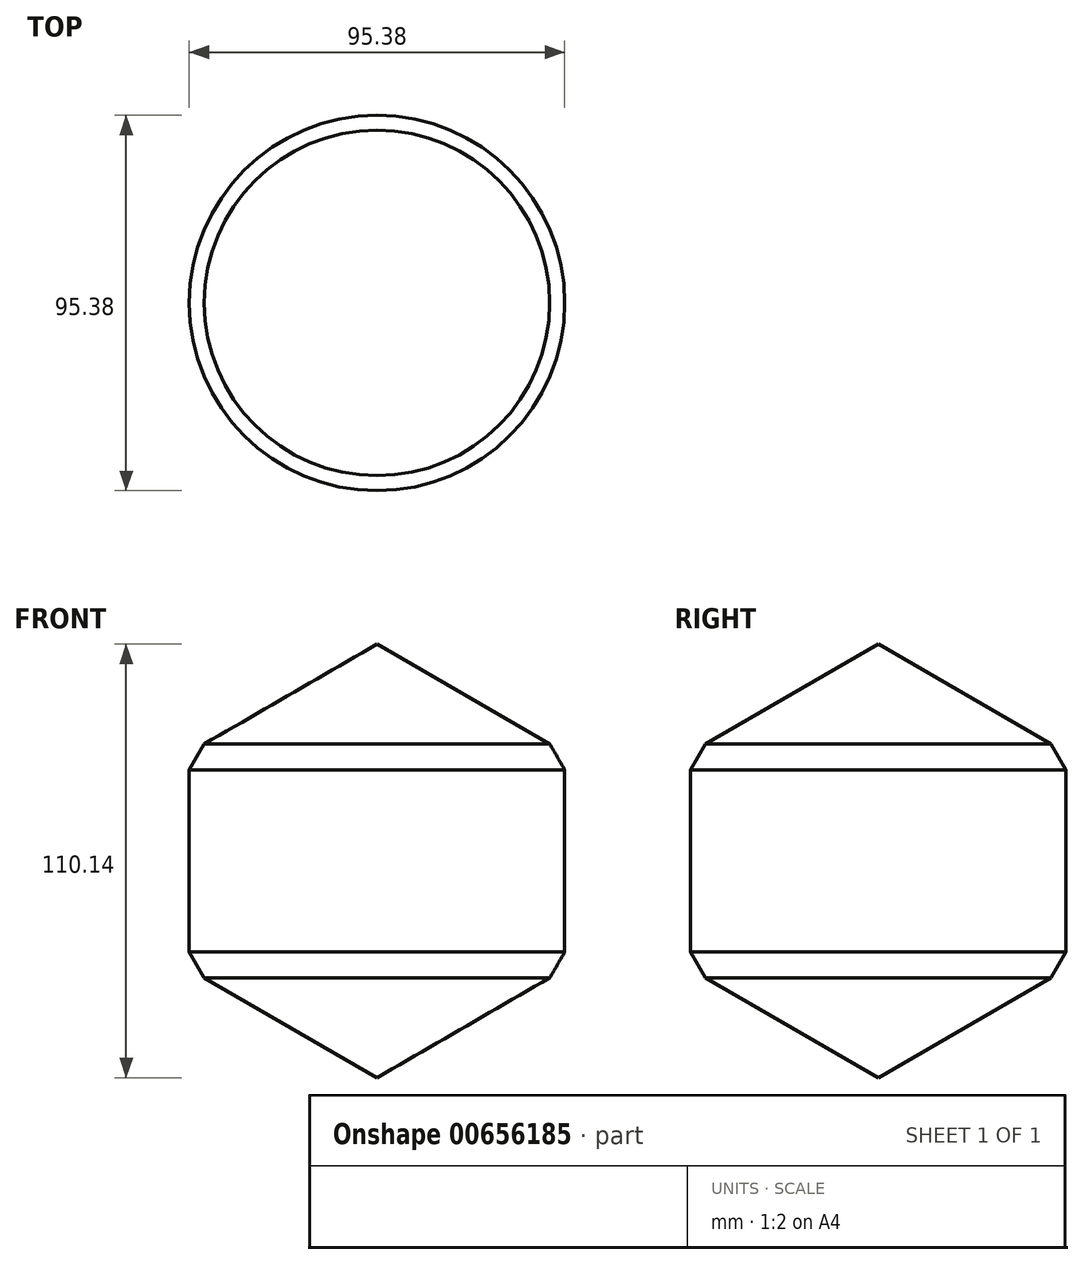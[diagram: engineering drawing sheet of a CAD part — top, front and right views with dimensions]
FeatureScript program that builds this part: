
annotation { "Feature Type Name" : "Feature", "Feature Type Description" : "" }
export const myFeature = defineFeature(function(context is Context, id is Id, definition is map)
    precondition{}
    {
        {
            var Q0;
            Q0=qCreatedBy(makeId("Front.planeOp"),FACE);
            var sketch = newSketch(context, id + "F0", { "sketchPlane" : qUnion([Q0])});
            skCircle(sketch, "E0.cCircle", {"center": v(0, 0) * mm, "radius": 55.07 * mm, "construction": true});
            skLineSegment(sketch, "E0.0", {"start": v(0, 55.07) * mm, "end": v(47.69, 27.53) * mm});
            skLineSegment(sketch, "E0.1", {"start": v(47.69, 27.53) * mm, "end": v(47.69, -27.53) * mm});
            skLineSegment(sketch, "E0.2", {"start": v(47.69, -27.53) * mm, "end": v(0, -55.07) * mm});
            skLineSegment(sketch, "E0.3", {"start": v(0, -55.07) * mm, "end": v(-47.69, -27.53) * mm});
            skLineSegment(sketch, "E0.4", {"start": v(-47.69, -27.53) * mm, "end": v(-47.69, 27.53) * mm});
            skLineSegment(sketch, "E0.5", {"start": v(-47.69, 27.53) * mm, "end": v(0, 55.07) * mm});
            skLineSegment(sketch, "E1", {"start": v(0, 55.07) * mm, "end": v(0, -55.07) * mm});
            skSolve(sketch);
        }
        {
            var Q0;
            Q0=makeQuery(id+"F0.imprint","IMPRINT",FACE,{"disambiguationData":[TD([[makeQuery(id+"F0.imprint","IMPRINT",EDGE,{"derivedFrom":sQuery(id+"F0.wireOp",EDGE,"E0.0")}),-1.0]])]});
            var Q1;
            Q1=sQuery(id+"F0.wireOp",EDGE,"E1");
            revolve(context, id + "F1", {"entities" : qUnion([Q0]), "axis" : qUnion([Q1]), "revolveType" : RevolveType.FULL});
        }
        {
            var Q0;
            Q0=makeQuery(id+"F1.opRevolve","SWEPT_EDGE",EDGE,{"disambiguationData":[OSD([sQuery(id+"F0.wireOp",EDGE,"E0.0"),sQuery(id+"F0.wireOp",EDGE,"E0.1")])]});
            var Q1;
            Q1=makeQuery(id+"F1.opRevolve","SWEPT_EDGE",EDGE,{"disambiguationData":[OSD([sQuery(id+"F0.wireOp",EDGE,"E0.1"),sQuery(id+"F0.wireOp",EDGE,"E0.2")])]});
            chamfer(context, id + "F2", {"entities" : qUnion([Q0, Q1]), "width" : 7.62 * mm, "tangentPropagation" : true});
        }
    });
